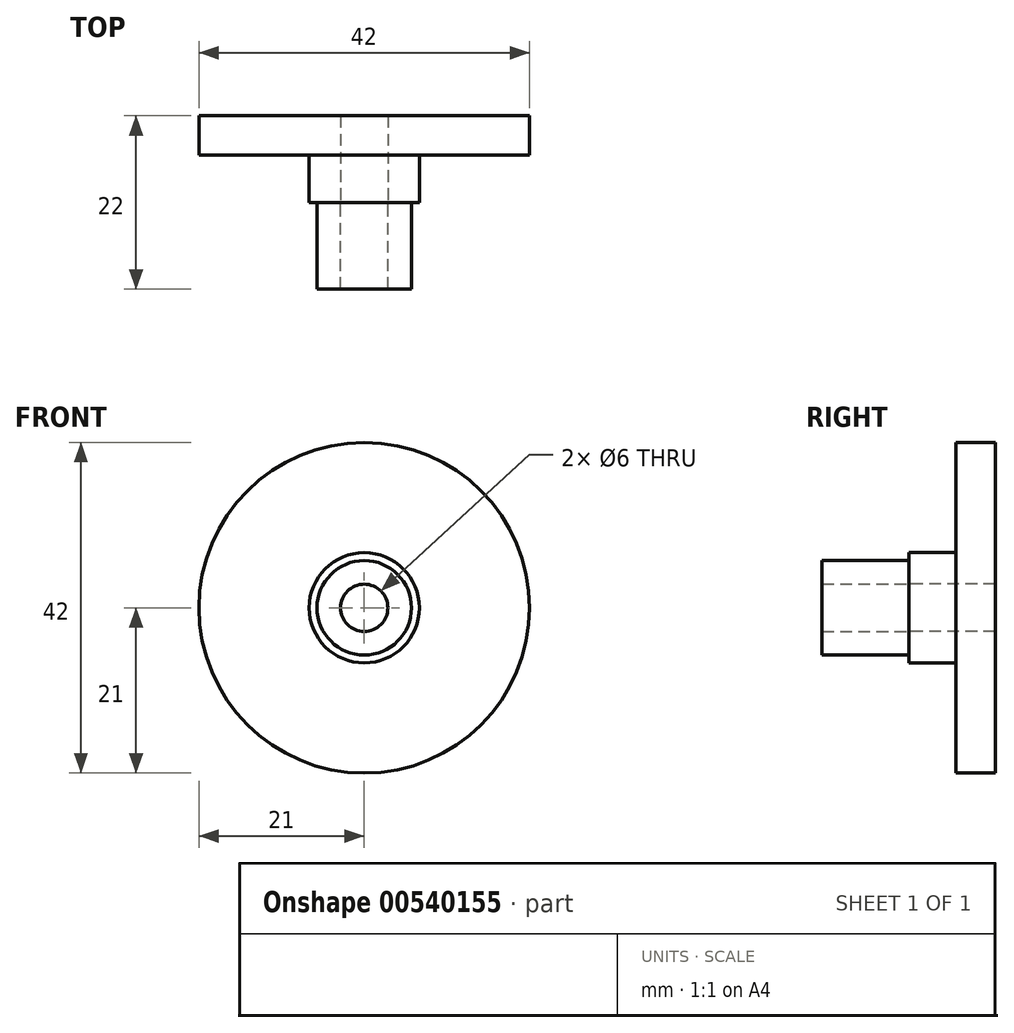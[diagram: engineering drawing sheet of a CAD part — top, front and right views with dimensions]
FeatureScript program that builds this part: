
annotation { "Feature Type Name" : "Feature", "Feature Type Description" : "" }
export const myFeature = defineFeature(function(context is Context, id is Id, definition is map)
    precondition{}
    {
        {
            var Q0;
            Q0=qCreatedBy(makeId("Right.planeOp"),FACE);
            var sketch = newSketch(context, id + "F0", { "sketchPlane" : qUnion([Q0])});
            skLineSegment(sketch, "E0", {"start": v(0, 0) * mm, "end": v(-11, 0) * mm, "construction": true});
            skLineSegment(sketch, "E1", {"start": v(0, 3) * mm, "end": v(-11, 3) * mm});
            skLineSegment(sketch, "E2", {"start": v(-11, 3) * mm, "end": v(-11, 6) * mm});
            skLineSegment(sketch, "E3", {"start": v(-11, 6) * mm, "end": v(0, 6) * mm});
            skLineSegment(sketch, "E4", {"start": v(0, 6) * mm, "end": v(0, 3) * mm});
            skSolve(sketch);
        }
        {
            var Q0;
            Q0 = qSketchRegion(id + "F0", true);
            var Q1;
            Q1=sQuery(id+"F0.wireOp",EDGE,"E0");
            revolve(context, id + "F1", {"entities" : qUnion([Q0]), "axis" : qUnion([Q1]), "revolveType" : RevolveType.FULL});
        }
        {
            var Q0;
            Q0=qCreatedBy(makeId("Right.planeOp"),FACE);
            var sketch = newSketch(context, id + "F2", { "sketchPlane" : qUnion([Q0])});
            skLineSegment(sketch, "E5", {"start": v(0, 0) * mm, "end": v(33.4, 0) * mm, "construction": true});
            skLineSegment(sketch, "E6", {"start": v(0, 3) * mm, "end": v(11, 3) * mm});
            skLineSegment(sketch, "E7", {"start": v(11, 3) * mm, "end": v(11, 21) * mm});
            skLineSegment(sketch, "E8", {"start": v(11, 21) * mm, "end": v(6, 21) * mm});
            skLineSegment(sketch, "E9", {"start": v(6, 21) * mm, "end": v(6, 7) * mm});
            skLineSegment(sketch, "E10", {"start": v(6, 7) * mm, "end": v(0, 7) * mm});
            skLineSegment(sketch, "E11", {"start": v(0, 7) * mm, "end": v(0, 3) * mm});
            skSolve(sketch);
        }
        {
            var Q0;
            Q0 = qSketchRegion(id + "F2", true);
            var Q1;
            Q1=sQuery(id+"F2.wireOp",EDGE,"E5");
            revolve(context, id + "F3", {"entities" : qUnion([Q0]), "axis" : qUnion([Q1]), "revolveType" : RevolveType.FULL});
        }
    });
